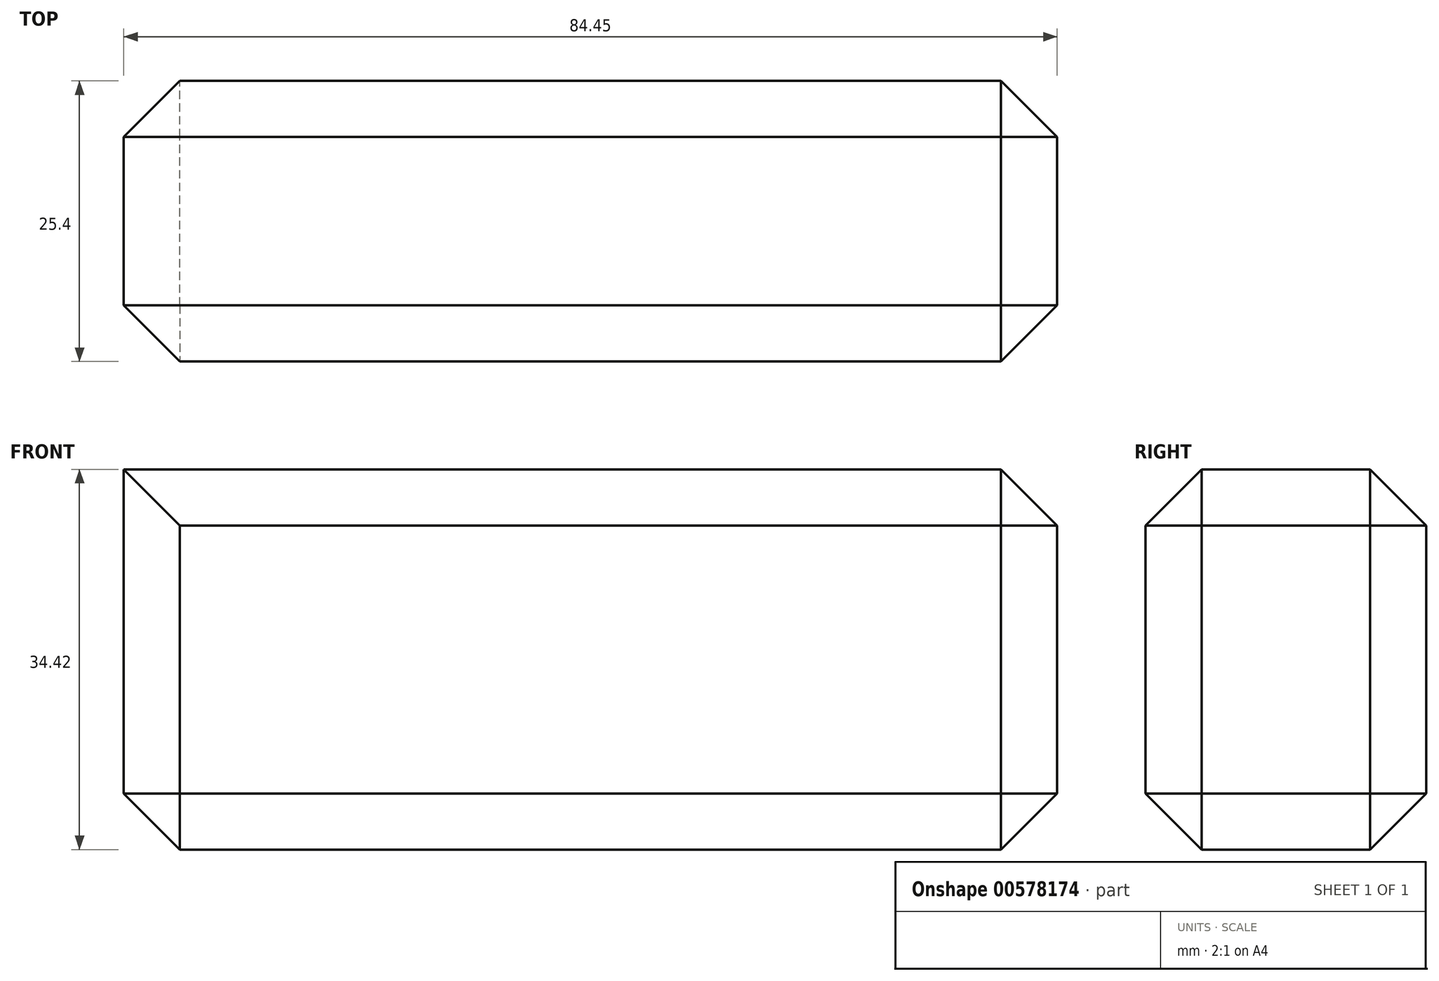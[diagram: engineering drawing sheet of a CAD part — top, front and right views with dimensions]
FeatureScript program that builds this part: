
annotation { "Feature Type Name" : "Feature", "Feature Type Description" : "" }
export const myFeature = defineFeature(function(context is Context, id is Id, definition is map)
    precondition{}
    {
        {
            var Q0;
            Q0=qCreatedBy(makeId("Front.planeOp"),FACE);
            var sketch = newSketch(context, id + "F0", { "sketchPlane" : qUnion([Q0])});
            skLineSegment(sketch, "E0.bottom", {"start": v(-35.55, 14.73) * mm, "end": v(48.9, 14.73) * mm});
            skLineSegment(sketch, "E0.top", {"start": v(-35.55, -19.7) * mm, "end": v(48.9, -19.7) * mm});
            skLineSegment(sketch, "E0.left", {"start": v(-35.55, 14.73) * mm, "end": v(-35.55, -19.7) * mm});
            skLineSegment(sketch, "E0.right", {"start": v(48.9, 14.73) * mm, "end": v(48.9, -19.7) * mm});
            skSolve(sketch);
        }
        {
            var Q0;
            Q0=makeQuery(id+"F0.imprint","IMPRINT",FACE,{"disambiguationData":[TD([[makeQuery(id+"F0.imprint","IMPRINT",EDGE,{"derivedFrom":sQuery(id+"F0.wireOp",EDGE,"E0.bottom")}),-1.0]])]});
            extrude(context, id + "F1", {"entities" : qUnion([Q0]), "depth" : 25.4 * mm, "offsetDistance" : 25.4 * mm});
        }
        {
            var Q0;
            Q0=makeQuery(id+"F1.opExtrude","SWEPT_EDGE",EDGE,{"disambiguationData":[OSD([sQuery(id+"F0.wireOp",EDGE,"E0.top"),sQuery(id+"F0.wireOp",EDGE,"E0.right")])]});
            var Q1;
            Q1=makeQuery(id+"F1.opExtrude","CAP_FACE",FACE,{"disambiguationData":[OSD([sQuery(id+"F0.wireOp",EDGE,"E0.bottom"),sQuery(id+"F0.wireOp",EDGE,"E0.top"),sQuery(id+"F0.wireOp",EDGE,"E0.left"),sQuery(id+"F0.wireOp",EDGE,"E0.right")])],"isStart":true});
            var Q2;
            Q2=makeQuery(id+"F1.opExtrude","SWEPT_FACE",FACE,{"disambiguationData":[OSD([sQuery(id+"F0.wireOp",EDGE,"E0.top")])]});
            var Q3;
            Q3=makeQuery(id+"F1.opExtrude","CAP_EDGE",EDGE,{"disambiguationData":[OSD([sQuery(id+"F0.wireOp",EDGE,"E0.top")])],"isStart":true});
            var Q4;
            Q4=makeQuery(id+"F1.opExtrude","SWEPT_FACE",FACE,{"disambiguationData":[OSD([sQuery(id+"F0.wireOp",EDGE,"E0.right")])]});
            var Q5;
            Q5=makeQuery(id+"F1.opExtrude","CAP_EDGE",EDGE,{"disambiguationData":[OSD([sQuery(id+"F0.wireOp",EDGE,"E0.right")])],"isStart":true});
            var Q6;
            Q6=makeQuery(id+"F1.opExtrude","CAP_EDGE",EDGE,{"disambiguationData":[OSD([sQuery(id+"F0.wireOp",EDGE,"E0.top")])],"isStart":false});
            var Q7;
            Q7=makeQuery(id+"F1.opExtrude","CAP_FACE",FACE,{"disambiguationData":[OSD([sQuery(id+"F0.wireOp",EDGE,"E0.bottom"),sQuery(id+"F0.wireOp",EDGE,"E0.top"),sQuery(id+"F0.wireOp",EDGE,"E0.left"),sQuery(id+"F0.wireOp",EDGE,"E0.right")])],"isStart":false});
            chamfer(context, id + "F2", {"entities" : qUnion([Q0, Q1, Q2, Q3, Q4, Q5, Q6, Q7]), "width" : 5.08 * mm, "tangentPropagation" : true});
        }
    });
